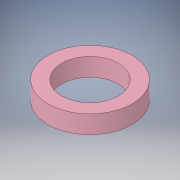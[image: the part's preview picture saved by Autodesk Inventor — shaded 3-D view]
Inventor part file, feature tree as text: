
AUTODESK INVENTOR PART (.ipt)
format: ipt  version: 2019 (Build 230136000, 136)  size: 111,104 bytes
history: native  units: mm
features: other x1, extrude x1, sketch x1
ambient origin geometry x8: Origin, YZ Plane, XZ Plane, XY Plane, X Axis, Y Axis, Z Axis, Center Point
bodies: Body1 (feature_tree)
feature tree (3):
  other  "Sólido1"
  extrude  "Extrusión1"  Depth=3.18mm
  sketch  "Boceto1"  dims[d0=10.0mm d1=14.8mm d2=3.18mm d3=0.0mm]
